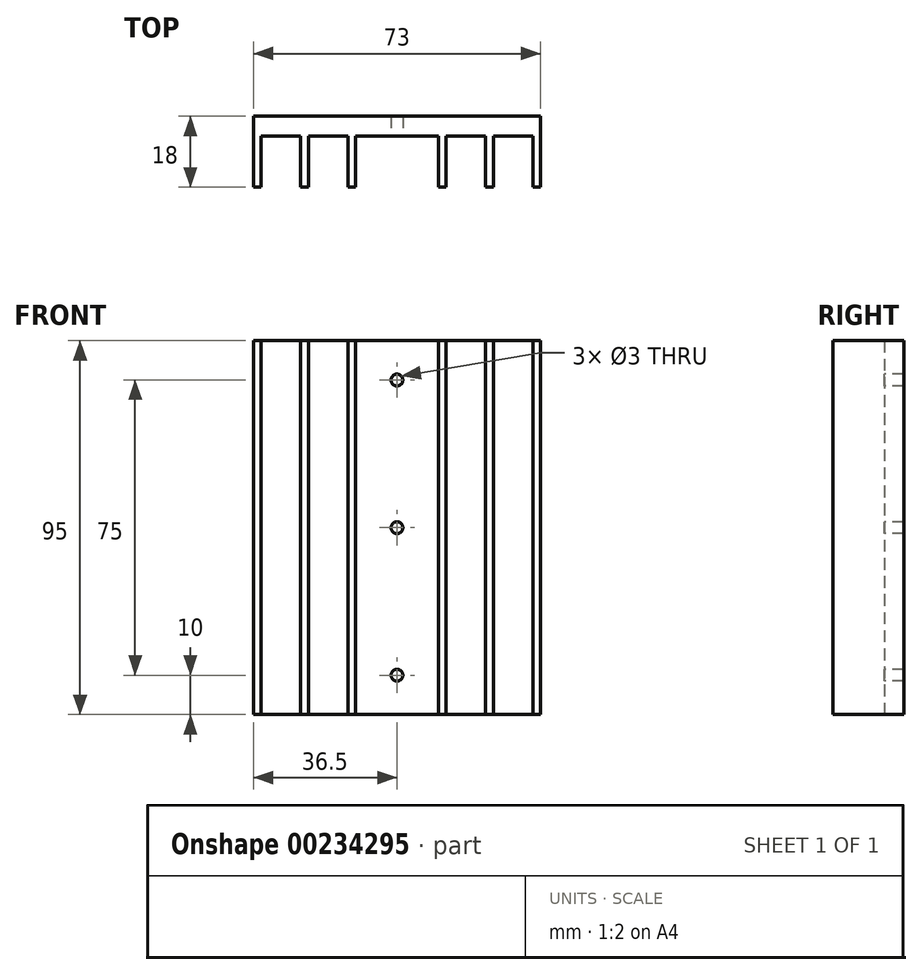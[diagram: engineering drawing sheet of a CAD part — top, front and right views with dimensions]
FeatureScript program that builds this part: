
annotation { "Feature Type Name" : "Feature", "Feature Type Description" : "" }
export const myFeature = defineFeature(function(context is Context, id is Id, definition is map)
    precondition{}
    {
        {
            var Q0;
            Q0=qCreatedBy(makeId("Top.planeOp"),FACE);
            var sketch = newSketch(context, id + "F0", { "sketchPlane" : qUnion([Q0])});
            skLineSegment(sketch, "E0", {"start": v(0, 0) * mm, "end": v(-36.5, 0) * mm});
            skLineSegment(sketch, "E1", {"start": v(-36.5, 0) * mm, "end": v(-36.5, -18) * mm});
            skLineSegment(sketch, "E2", {"start": v(-36.5, -18) * mm, "end": v(-34.5, -18) * mm});
            skLineSegment(sketch, "E3", {"start": v(-34.5, -18) * mm, "end": v(-34.5, -5) * mm});
            skLineSegment(sketch, "E4", {"start": v(-34.5, -5) * mm, "end": v(-24.5, -5) * mm});
            skLineSegment(sketch, "E5", {"start": v(-24.5, -5) * mm, "end": v(-24.5, -18) * mm});
            skLineSegment(sketch, "E6", {"start": v(-24.5, -18) * mm, "end": v(-22.5, -18) * mm});
            skLineSegment(sketch, "E7", {"start": v(-22.5, -18) * mm, "end": v(-22.5, -5) * mm});
            skLineSegment(sketch, "E8", {"start": v(-22.5, -5) * mm, "end": v(-12.5, -5) * mm});
            skLineSegment(sketch, "E9", {"start": v(-12.5, -5) * mm, "end": v(-12.5, -18) * mm});
            skLineSegment(sketch, "E10", {"start": v(-12.5, -18) * mm, "end": v(-10.5, -18) * mm});
            skLineSegment(sketch, "E11", {"start": v(-10.5, -18) * mm, "end": v(-10.5, -5) * mm});
            skLineSegment(sketch, "E12", {"start": v(-10.5, -5) * mm, "end": v(0, -5) * mm});
            skLineSegment(sketch, "E13", {"start": v(0, 6.05) * mm, "end": v(0, -11.22) * mm, "construction": true});
            skLineSegment(sketch, "E14.MirrorCS", {"start": v(24.5, -18) * mm, "end": v(22.5, -18) * mm});
            skLineSegment(sketch, "E15.MirrorCS", {"start": v(12.5, -18) * mm, "end": v(10.5, -18) * mm});
            skLineSegment(sketch, "E16.MirrorCS", {"start": v(36.5, -18) * mm, "end": v(34.5, -18) * mm});
            skLineSegment(sketch, "E17.MirrorCS", {"start": v(12.5, -5) * mm, "end": v(12.5, -18) * mm});
            skLineSegment(sketch, "E18.MirrorCS", {"start": v(34.5, -5) * mm, "end": v(24.5, -5) * mm});
            skLineSegment(sketch, "E19.MirrorCS", {"start": v(34.5, -18) * mm, "end": v(34.5, -5) * mm});
            skLineSegment(sketch, "E20.MirrorCS", {"start": v(22.5, -5) * mm, "end": v(12.5, -5) * mm});
            skLineSegment(sketch, "E21.MirrorCS", {"start": v(22.5, -18) * mm, "end": v(22.5, -5) * mm});
            skLineSegment(sketch, "E22.MirrorCS", {"start": v(24.5, -5) * mm, "end": v(24.5, -18) * mm});
            skLineSegment(sketch, "E23.MirrorCS", {"start": v(36.5, 0) * mm, "end": v(36.5, -18) * mm});
            skLineSegment(sketch, "E24.MirrorCS", {"start": v(10.5, -18) * mm, "end": v(10.5, -5) * mm});
            skLineSegment(sketch, "E25.MirrorCS", {"start": v(10.5, -5) * mm, "end": v(0, -5) * mm});
            skLineSegment(sketch, "E26.MirrorCS", {"start": v(0, 0) * mm, "end": v(36.5, 0) * mm});
            skSolve(sketch);
        }
        {
            var Q0;
            Q0 = qSketchRegion(id + "F0", true);
            extrude(context, id + "F1", {"entities" : qUnion([Q0]), "depth" : 95 * mm});
        }
        {
            var Q0;
            Q0=makeQuery(id+"F1.opExtrude","SWEPT_FACE",FACE,{"disambiguationData":[OSD([sQuery(id+"F0.wireOp",EDGE,"E12"),sQuery(id+"F0.wireOp",EDGE,"E25.MirrorCS")])]});
            var sketch = newSketch(context, id + "F2", { "sketchPlane" : qUnion([Q0])});
            skLineSegment(sketch, "E27", {"start": v(0, 0) * mm, "end": v(0, 95) * mm, "construction": true});
            skCircle(sketch, "E28", {"center": v(0, 10) * mm, "radius": 1.5 * mm});
            skCircle(sketch, "E29", {"center": v(0, 47.5) * mm, "radius": 1.5 * mm});
            skCircle(sketch, "E30", {"center": v(0, 85) * mm, "radius": 1.5 * mm});
            skSolve(sketch);
        }
        {
            var Q0;
            Q0=makeQuery(id+"F2.imprint","IMPRINT",FACE,{"disambiguationData":[TD([[makeQuery(id+"F2.imprint","IMPRINT",EDGE,{"derivedFrom":sQuery(id+"F2.wireOp",EDGE,"E30")}),1.0]])]});
            var Q1;
            Q1=makeQuery(id+"F2.imprint","IMPRINT",FACE,{"disambiguationData":[TD([[makeQuery(id+"F2.imprint","IMPRINT",EDGE,{"derivedFrom":sQuery(id+"F2.wireOp",EDGE,"E29")}),1.0]])]});
            var Q2;
            Q2=makeQuery(id+"F2.imprint","IMPRINT",FACE,{"disambiguationData":[TD([[makeQuery(id+"F2.imprint","IMPRINT",EDGE,{"derivedFrom":sQuery(id+"F2.wireOp",EDGE,"E28")}),1.0]])]});
            var Q3;
            Q3=sQuery(id+"F2.wireOp",EDGE,"E30");
            var Q4;
            Q4=sQuery(id+"F2.wireOp",EDGE,"E29");
            var Q5;
            Q5=sQuery(id+"F2.wireOp",EDGE,"E28");
            extrude(context, id + "F3", {"entities" : qUnion([Q0, Q1, Q2]), "operationType" : NewBodyOperationType.REMOVE, "surfaceEntities" : qUnion([Q3, Q4, Q5]), "endBound" : BoundingType.UP_TO_NEXT, "oppositeDirection" : true, "depth" : 25 * mm});
        }
    });
